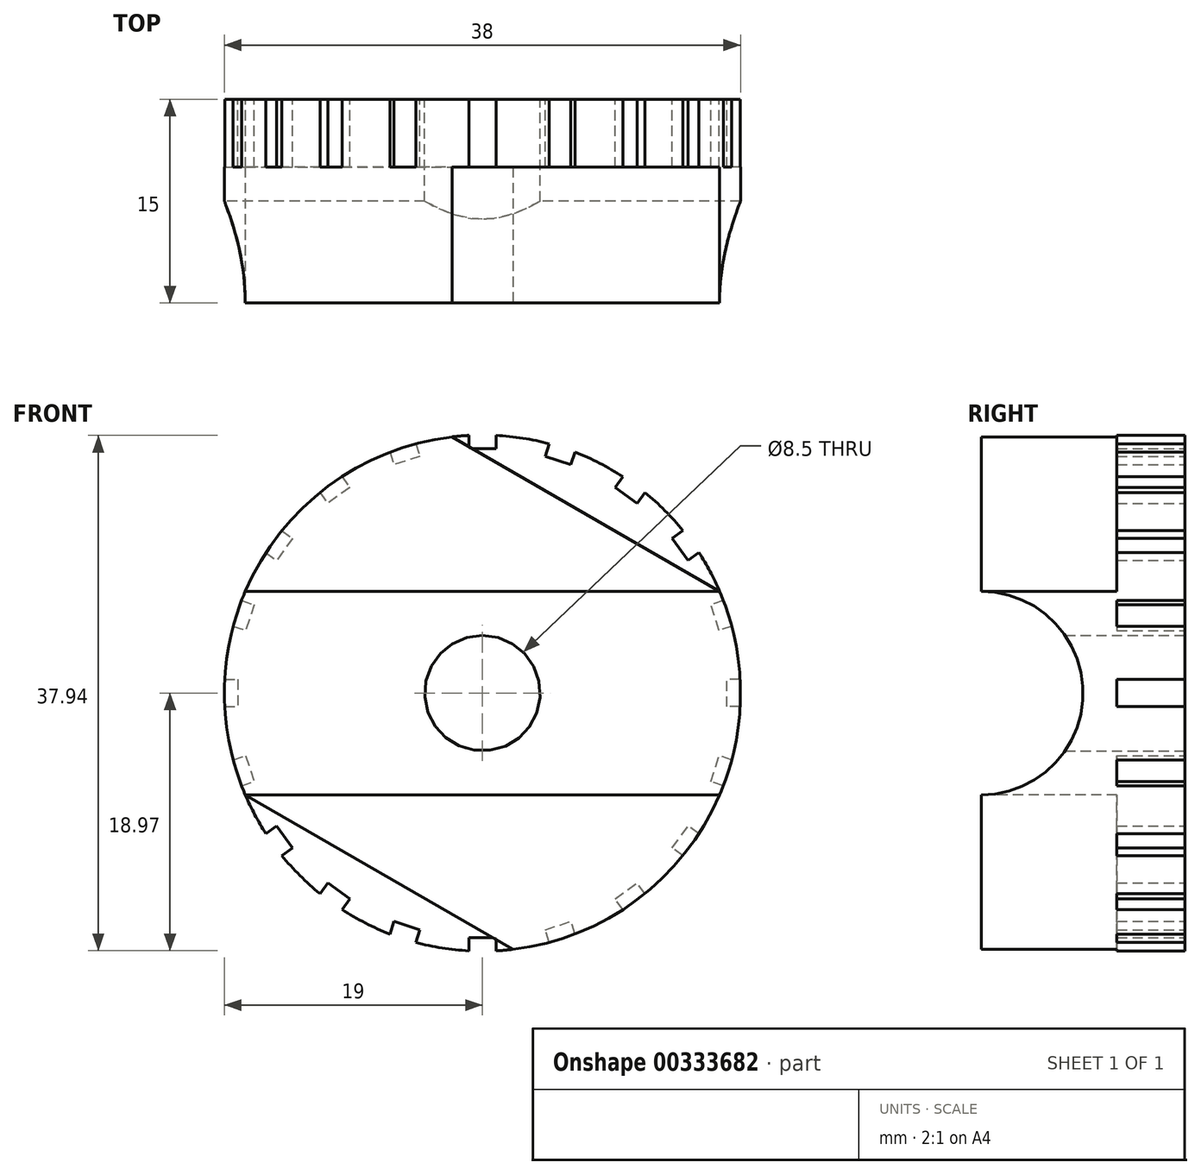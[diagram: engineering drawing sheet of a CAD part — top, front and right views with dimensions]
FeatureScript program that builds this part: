
annotation { "Feature Type Name" : "Feature", "Feature Type Description" : "" }
export const myFeature = defineFeature(function(context is Context, id is Id, definition is map)
    precondition{}
    {
        {
            var Q0;
            Q0=qCreatedBy(makeId("Front.planeOp"),FACE);
            var sketch = newSketch(context, id + "F0", { "sketchPlane" : qUnion([Q0])});
            skCircle(sketch, "E0", {"center": v(0, 0) * mm, "radius": 4.25 * mm});
            skCircle(sketch, "E1", {"center": v(0, 0) * mm, "radius": 19 * mm});
            skSolve(sketch);
        }
        {
            var Q0;
            Q0 = qSketchRegion(id + "F0", true);
            extrude(context, id + "F1", {"entities" : qUnion([Q0]), "depth" : 15 * mm});
        }
        {
            var Q0;
            Q0=qCreatedBy(makeId("Right.planeOp"),FACE);
            var sketch = newSketch(context, id + "F2", { "sketchPlane" : qUnion([Q0])});
            skLineSegment(sketch, "E2", {"start": v(0, 0) * mm, "end": v(-15, 0) * mm});
            skCircle(sketch, "E3", {"center": v(-15, 0) * mm, "radius": 7.5 * mm});
            skSolve(sketch);
        }
        {
            var Q0;
            Q0 = qSketchRegion(id + "F2", true);
            extrude(context, id + "F3", {"entities" : qUnion([Q0]), "operationType" : NewBodyOperationType.REMOVE, "endBound" : BoundingType.THROUGH_ALL, "depth" : 25 * mm, "hasSecondDirection" : true, "secondDirectionBound" : SecondDirectionBoundingType.THROUGH_ALL, "secondDirectionOppositeDirection" : true, "secondDirectionDepth" : 25 * mm});
        }
        {
            var Q0;
            Q0=qCreatedBy(makeId("Front.planeOp"),FACE);
            var sketch = newSketch(context, id + "F4", { "sketchPlane" : qUnion([Q0])});
            skLineSegment(sketch, "E4.bottom", {"start": v(20, -1) * mm, "end": v(18, -1) * mm});
            skLineSegment(sketch, "E4.top", {"start": v(20, 1) * mm, "end": v(18, 1) * mm});
            skLineSegment(sketch, "E4.left", {"start": v(20, -1) * mm, "end": v(20, 1) * mm});
            skLineSegment(sketch, "E4.right", {"start": v(18, -1) * mm, "end": v(18, 1) * mm});
            skPoint(sketch, "E4.middle", {"position": v(19, 0) * mm});
            skLineSegment(sketch, "E5.1.0", {"start": v(17.43, 4.61) * mm, "end": v(16.81, 6.51) * mm});
            skLineSegment(sketch, "E5.1.1", {"start": v(19.33, 5.23) * mm, "end": v(17.43, 4.61) * mm});
            skLineSegment(sketch, "E5.1.2", {"start": v(19.33, 5.23) * mm, "end": v(18.71, 7.13) * mm});
            skLineSegment(sketch, "E5.1.3", {"start": v(18.71, 7.13) * mm, "end": v(16.81, 6.51) * mm});
            skLineSegment(sketch, "E5.2.0", {"start": v(15.15, 9.77) * mm, "end": v(13.97, 11.39) * mm});
            skLineSegment(sketch, "E5.2.1", {"start": v(16.77, 10.95) * mm, "end": v(15.15, 9.77) * mm});
            skLineSegment(sketch, "E5.2.2", {"start": v(16.77, 10.95) * mm, "end": v(15.6, 12.56) * mm});
            skLineSegment(sketch, "E5.2.3", {"start": v(15.6, 12.56) * mm, "end": v(13.97, 11.39) * mm});
            skLineSegment(sketch, "E5.3.0", {"start": v(11.39, 13.97) * mm, "end": v(9.77, 15.15) * mm});
            skLineSegment(sketch, "E5.3.1", {"start": v(12.56, 15.6) * mm, "end": v(11.39, 13.97) * mm});
            skLineSegment(sketch, "E5.3.2", {"start": v(12.56, 15.6) * mm, "end": v(10.95, 16.77) * mm});
            skLineSegment(sketch, "E5.3.3", {"start": v(10.95, 16.77) * mm, "end": v(9.77, 15.15) * mm});
            skLineSegment(sketch, "E5.4.0", {"start": v(6.51, 16.81) * mm, "end": v(4.61, 17.43) * mm});
            skLineSegment(sketch, "E5.4.1", {"start": v(7.13, 18.71) * mm, "end": v(6.51, 16.81) * mm});
            skLineSegment(sketch, "E5.4.2", {"start": v(7.13, 18.71) * mm, "end": v(5.23, 19.33) * mm});
            skLineSegment(sketch, "E5.4.3", {"start": v(5.23, 19.33) * mm, "end": v(4.61, 17.43) * mm});
            skLineSegment(sketch, "E5.5.0", {"start": v(1, 18) * mm, "end": v(-1, 18) * mm});
            skLineSegment(sketch, "E5.5.1", {"start": v(1, 20) * mm, "end": v(1, 18) * mm});
            skLineSegment(sketch, "E5.5.2", {"start": v(1, 20) * mm, "end": v(-1, 20) * mm});
            skLineSegment(sketch, "E5.5.3", {"start": v(-1, 20) * mm, "end": v(-1, 18) * mm});
            skLineSegment(sketch, "E5.6.0", {"start": v(-4.61, 17.43) * mm, "end": v(-6.51, 16.81) * mm});
            skLineSegment(sketch, "E5.6.1", {"start": v(-5.23, 19.33) * mm, "end": v(-4.61, 17.43) * mm});
            skLineSegment(sketch, "E5.6.2", {"start": v(-5.23, 19.33) * mm, "end": v(-7.13, 18.71) * mm});
            skLineSegment(sketch, "E5.6.3", {"start": v(-7.13, 18.71) * mm, "end": v(-6.51, 16.81) * mm});
            skLineSegment(sketch, "E5.7.0", {"start": v(-9.77, 15.15) * mm, "end": v(-11.39, 13.97) * mm});
            skLineSegment(sketch, "E5.7.1", {"start": v(-10.95, 16.77) * mm, "end": v(-9.77, 15.15) * mm});
            skLineSegment(sketch, "E5.7.2", {"start": v(-10.95, 16.77) * mm, "end": v(-12.56, 15.6) * mm});
            skLineSegment(sketch, "E5.7.3", {"start": v(-12.56, 15.6) * mm, "end": v(-11.39, 13.97) * mm});
            skLineSegment(sketch, "E5.8.0", {"start": v(-13.97, 11.39) * mm, "end": v(-15.15, 9.77) * mm});
            skLineSegment(sketch, "E5.8.1", {"start": v(-15.6, 12.56) * mm, "end": v(-13.97, 11.39) * mm});
            skLineSegment(sketch, "E5.8.2", {"start": v(-15.6, 12.56) * mm, "end": v(-16.77, 10.95) * mm});
            skLineSegment(sketch, "E5.8.3", {"start": v(-16.77, 10.95) * mm, "end": v(-15.15, 9.77) * mm});
            skLineSegment(sketch, "E5.9.0", {"start": v(-16.81, 6.51) * mm, "end": v(-17.43, 4.61) * mm});
            skLineSegment(sketch, "E5.9.1", {"start": v(-18.71, 7.13) * mm, "end": v(-16.81, 6.51) * mm});
            skLineSegment(sketch, "E5.9.2", {"start": v(-18.71, 7.13) * mm, "end": v(-19.33, 5.23) * mm});
            skLineSegment(sketch, "E5.9.3", {"start": v(-19.33, 5.23) * mm, "end": v(-17.43, 4.61) * mm});
            skLineSegment(sketch, "E5.10.0", {"start": v(-18, 1) * mm, "end": v(-18, -1) * mm});
            skLineSegment(sketch, "E5.10.1", {"start": v(-20, 1) * mm, "end": v(-18, 1) * mm});
            skLineSegment(sketch, "E5.10.2", {"start": v(-20, 1) * mm, "end": v(-20, -1) * mm});
            skLineSegment(sketch, "E5.10.3", {"start": v(-20, -1) * mm, "end": v(-18, -1) * mm});
            skLineSegment(sketch, "E5.11.0", {"start": v(-17.43, -4.61) * mm, "end": v(-16.81, -6.51) * mm});
            skLineSegment(sketch, "E5.11.1", {"start": v(-19.33, -5.23) * mm, "end": v(-17.43, -4.61) * mm});
            skLineSegment(sketch, "E5.11.2", {"start": v(-19.33, -5.23) * mm, "end": v(-18.71, -7.13) * mm});
            skLineSegment(sketch, "E5.11.3", {"start": v(-18.71, -7.13) * mm, "end": v(-16.81, -6.51) * mm});
            skLineSegment(sketch, "E5.12.0", {"start": v(-15.15, -9.77) * mm, "end": v(-13.97, -11.39) * mm});
            skLineSegment(sketch, "E5.12.1", {"start": v(-16.77, -10.95) * mm, "end": v(-15.15, -9.77) * mm});
            skLineSegment(sketch, "E5.12.2", {"start": v(-16.77, -10.95) * mm, "end": v(-15.6, -12.56) * mm});
            skLineSegment(sketch, "E5.12.3", {"start": v(-15.6, -12.56) * mm, "end": v(-13.97, -11.39) * mm});
            skLineSegment(sketch, "E5.13.0", {"start": v(-11.39, -13.97) * mm, "end": v(-9.77, -15.15) * mm});
            skLineSegment(sketch, "E5.13.1", {"start": v(-12.56, -15.6) * mm, "end": v(-11.39, -13.97) * mm});
            skLineSegment(sketch, "E5.13.2", {"start": v(-12.56, -15.6) * mm, "end": v(-10.95, -16.77) * mm});
            skLineSegment(sketch, "E5.13.3", {"start": v(-10.95, -16.77) * mm, "end": v(-9.77, -15.15) * mm});
            skLineSegment(sketch, "E5.14.0", {"start": v(-6.51, -16.81) * mm, "end": v(-4.61, -17.43) * mm});
            skLineSegment(sketch, "E5.14.1", {"start": v(-7.13, -18.71) * mm, "end": v(-6.51, -16.81) * mm});
            skLineSegment(sketch, "E5.14.2", {"start": v(-7.13, -18.71) * mm, "end": v(-5.23, -19.33) * mm});
            skLineSegment(sketch, "E5.14.3", {"start": v(-5.23, -19.33) * mm, "end": v(-4.61, -17.43) * mm});
            skLineSegment(sketch, "E5.15.0", {"start": v(-1, -18) * mm, "end": v(1, -18) * mm});
            skLineSegment(sketch, "E5.15.1", {"start": v(-1, -20) * mm, "end": v(-1, -18) * mm});
            skLineSegment(sketch, "E5.15.2", {"start": v(-1, -20) * mm, "end": v(1, -20) * mm});
            skLineSegment(sketch, "E5.15.3", {"start": v(1, -20) * mm, "end": v(1, -18) * mm});
            skLineSegment(sketch, "E5.16.0", {"start": v(4.61, -17.43) * mm, "end": v(6.51, -16.81) * mm});
            skLineSegment(sketch, "E5.16.1", {"start": v(5.23, -19.33) * mm, "end": v(4.61, -17.43) * mm});
            skLineSegment(sketch, "E5.16.2", {"start": v(5.23, -19.33) * mm, "end": v(7.13, -18.71) * mm});
            skLineSegment(sketch, "E5.16.3", {"start": v(7.13, -18.71) * mm, "end": v(6.51, -16.81) * mm});
            skLineSegment(sketch, "E5.17.0", {"start": v(9.77, -15.15) * mm, "end": v(11.39, -13.97) * mm});
            skLineSegment(sketch, "E5.17.1", {"start": v(10.95, -16.77) * mm, "end": v(9.77, -15.15) * mm});
            skLineSegment(sketch, "E5.17.2", {"start": v(10.95, -16.77) * mm, "end": v(12.56, -15.6) * mm});
            skLineSegment(sketch, "E5.17.3", {"start": v(12.56, -15.6) * mm, "end": v(11.39, -13.97) * mm});
            skLineSegment(sketch, "E5.18.0", {"start": v(13.97, -11.39) * mm, "end": v(15.15, -9.77) * mm});
            skLineSegment(sketch, "E5.18.1", {"start": v(15.6, -12.56) * mm, "end": v(13.97, -11.39) * mm});
            skLineSegment(sketch, "E5.18.2", {"start": v(15.6, -12.56) * mm, "end": v(16.77, -10.95) * mm});
            skLineSegment(sketch, "E5.18.3", {"start": v(16.77, -10.95) * mm, "end": v(15.15, -9.77) * mm});
            skLineSegment(sketch, "E5.19.0", {"start": v(16.81, -6.51) * mm, "end": v(17.43, -4.61) * mm});
            skLineSegment(sketch, "E5.19.1", {"start": v(18.71, -7.13) * mm, "end": v(16.81, -6.51) * mm});
            skLineSegment(sketch, "E5.19.2", {"start": v(18.71, -7.13) * mm, "end": v(19.33, -5.23) * mm});
            skLineSegment(sketch, "E5.19.3", {"start": v(19.33, -5.23) * mm, "end": v(17.43, -4.61) * mm});
            skPoint(sketch, "E5.center", {"position": v(0, 0) * mm});
            skSolve(sketch);
        }
        {
            var Q0;
            Q0 = qSketchRegion(id + "F4", true);
            extrude(context, id + "F5", {"entities" : qUnion([Q0]), "operationType" : NewBodyOperationType.REMOVE, "depth" : 5 * mm});
        }
        {
            var Q0;
            Q0=makeQuery(id+"FleA5mUiALwIZy2_1.1.F3.boolean.opBoolean","SPLIT",FACE,{"disambiguationData":[OD(1.0)],"derivedFrom":makeQuery(id+"F3.boolean.opBoolean","SPLIT",FACE,{"disambiguationData":[OD(1.0)],"derivedFrom":makeQuery(id+"F1.opExtrude","CAP_FACE",FACE,{"disambiguationData":[OSD([sQuery(id+"F0.wireOp",EDGE,"E0"),sQuery(id+"F0.wireOp",EDGE,"E1")])],"isStart":false})})});
            var sketch = newSketch(context, id + "F6", { "sketchPlane" : qUnion([Q0])});
            skArc(sketch, "E6", {"start": v(-17.46, -7.5) * mm, "mid": v(-9.5, -16.45) * mm, "end": v(2.23, -18.87) * mm});
            skLineSegment(sketch, "E7", {"start": v(-2.23, 18.87) * mm, "end": v(17.46, 7.5) * mm});
            skLineSegment(sketch, "E8", {"start": v(2.23, -18.87) * mm, "end": v(-17.46, -7.5) * mm});
            skArc(sketch, "E9.trimOffspring", {"start": v(17.46, 7.5) * mm, "mid": v(9.5, 16.45) * mm, "end": v(-2.23, 18.87) * mm});
            skSolve(sketch);
        }
        {
            var Q0;
            Q0 = qSketchRegion(id + "F6", true);
            extrude(context, id + "F7", {"entities" : qUnion([Q0]), "operationType" : NewBodyOperationType.REMOVE, "oppositeDirection" : true, "depth" : 10 * mm});
        }
    });
